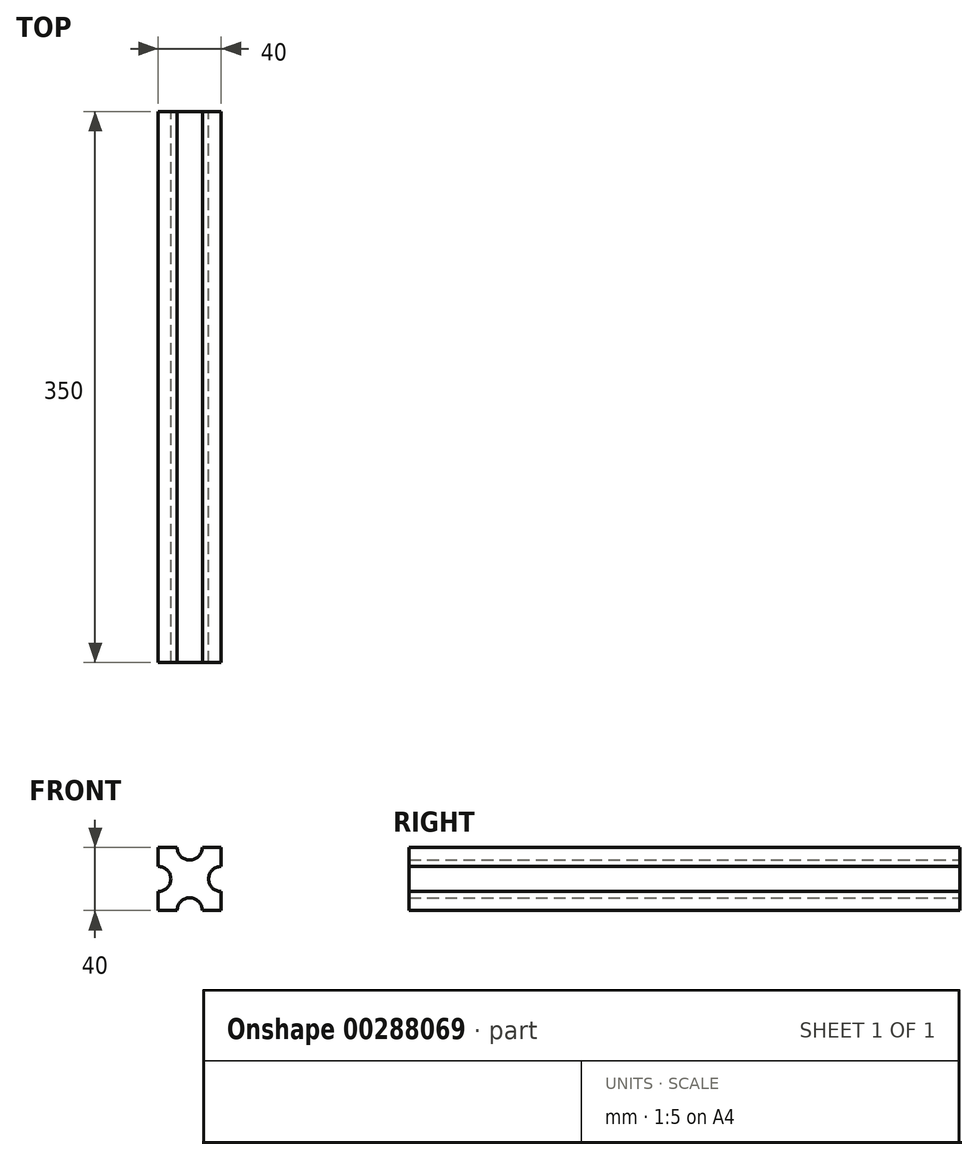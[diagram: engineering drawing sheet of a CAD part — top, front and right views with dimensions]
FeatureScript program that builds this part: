
annotation { "Feature Type Name" : "Feature", "Feature Type Description" : "" }
export const myFeature = defineFeature(function(context is Context, id is Id, definition is map)
    precondition{}
    {
        {
            var Q0;
            Q0=qCreatedBy(makeId("Front.planeOp"),FACE);
            var sketch = newSketch(context, id + "F0", { "sketchPlane" : qUnion([Q0])});
            skLineSegment(sketch, "E0.bottom", {"start": v(20, -20) * mm, "end": v(-20, -20) * mm});
            skLineSegment(sketch, "E0.top", {"start": v(20, 20) * mm, "end": v(-20, 20) * mm});
            skLineSegment(sketch, "E0.left", {"start": v(20, -20) * mm, "end": v(20, 20) * mm});
            skLineSegment(sketch, "E0.right", {"start": v(-20, -20) * mm, "end": v(-20, 20) * mm});
            skPoint(sketch, "E0.middle", {"position": v(0, 0) * mm});
            skCircle(sketch, "E1", {"center": v(0, 20) * mm, "radius": 8 * mm});
            skCircle(sketch, "E2", {"center": v(-20, 0) * mm, "radius": 8 * mm});
            skCircle(sketch, "E3", {"center": v(0, -20) * mm, "radius": 8 * mm});
            skCircle(sketch, "E4", {"center": v(20, 0) * mm, "radius": 8 * mm});
            skSolve(sketch);
        }
        {
            var Q0;
            {var subQ4=sQuery(id+"F0.wireOp",EDGE,"E0.bottom");var subQ6=sQuery(id+"F0.wireOp",EDGE,"E0.left");var subQ11=makeQuery(id+"F0.imprint","INTERSECT",VERTEX,{"derivedFrom":[subQ4,subQ6]});Q0=makeQuery(id+"F0.imprint","IMPRINT",FACE,{"disambiguationData":[TD([[makeQuery(id+"F0.imprint","IMPRINT",EDGE,{"disambiguationData":[TD([[subQ11,-1.0]])],"derivedFrom":subQ4}),-1.0]])]});}
            extrude(context, id + "F1", {"entities" : qUnion([Q0]), "depth" : 350 * mm});
        }
    });
